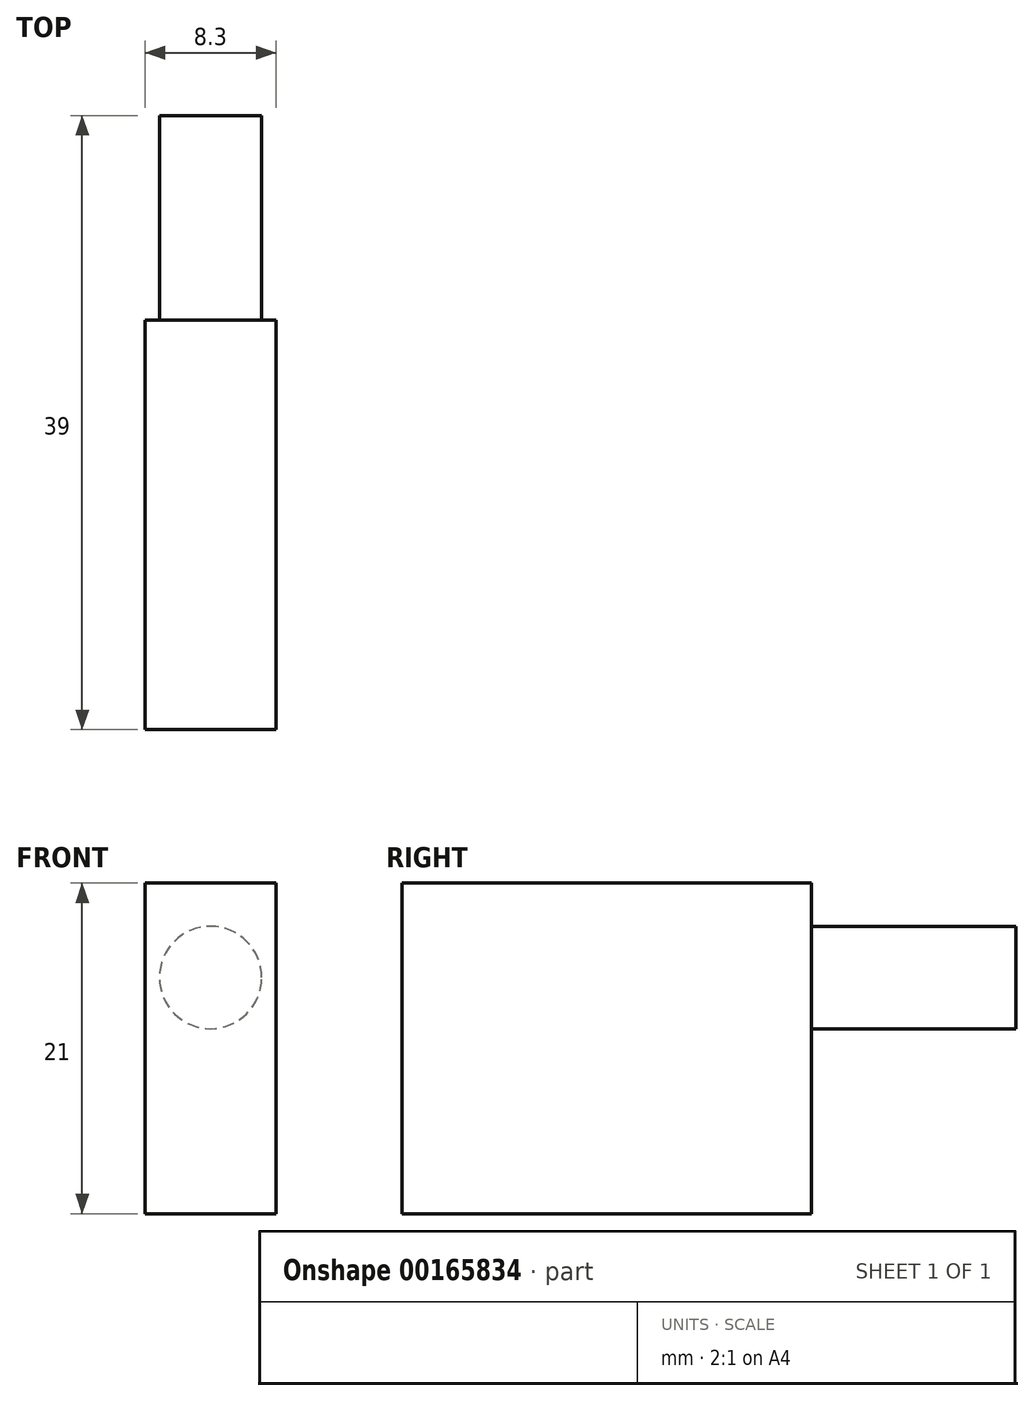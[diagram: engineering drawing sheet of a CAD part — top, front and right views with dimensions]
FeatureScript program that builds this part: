
annotation { "Feature Type Name" : "Feature", "Feature Type Description" : "" }
export const myFeature = defineFeature(function(context is Context, id is Id, definition is map)
    precondition{}
    {
        {
            var Q0;
            Q0=qCreatedBy(makeId("Right.planeOp"),FACE);
            var sketch = newSketch(context, id + "F0", { "sketchPlane" : qUnion([Q0])});
            skLineSegment(sketch, "E0.bottom", {"start": v(13, 10.5) * mm, "end": v(-13, 10.5) * mm});
            skLineSegment(sketch, "E0.top", {"start": v(13, -10.5) * mm, "end": v(-13, -10.5) * mm});
            skLineSegment(sketch, "E0.left", {"start": v(13, 10.5) * mm, "end": v(13, -10.5) * mm});
            skLineSegment(sketch, "E0.right", {"start": v(-13, 10.5) * mm, "end": v(-13, -10.5) * mm});
            skPoint(sketch, "E0.middle", {"position": v(0, 0) * mm});
            skSolve(sketch);
        }
        {
            var Q0;
            Q0 = qSketchRegion(id + "F0", true);
            extrude(context, id + "F1", {"entities" : qUnion([Q0]), "endBound" : BoundingType.SYMMETRIC, "depth" : 8.3 * mm});
        }
        {
            var Q0;
            Q0=makeQuery(id+"F1.opExtrude","SWEPT_FACE",FACE,{"disambiguationData":[OSD([sQuery(id+"F0.wireOp",EDGE,"E0.left")])]});
            var sketch = newSketch(context, id + "F2", { "sketchPlane" : qUnion([Q0])});
            skCircle(sketch, "E1", {"center": v(0, 4.5) * mm, "radius": 3.25 * mm});
            skSolve(sketch);
        }
        {
            var Q0;
            Q0 = qSketchRegion(id + "F2", true);
            extrude(context, id + "F3", {"entities" : qUnion([Q0]), "operationType" : NewBodyOperationType.ADD, "depth" : 13 * mm});
        }
    });
